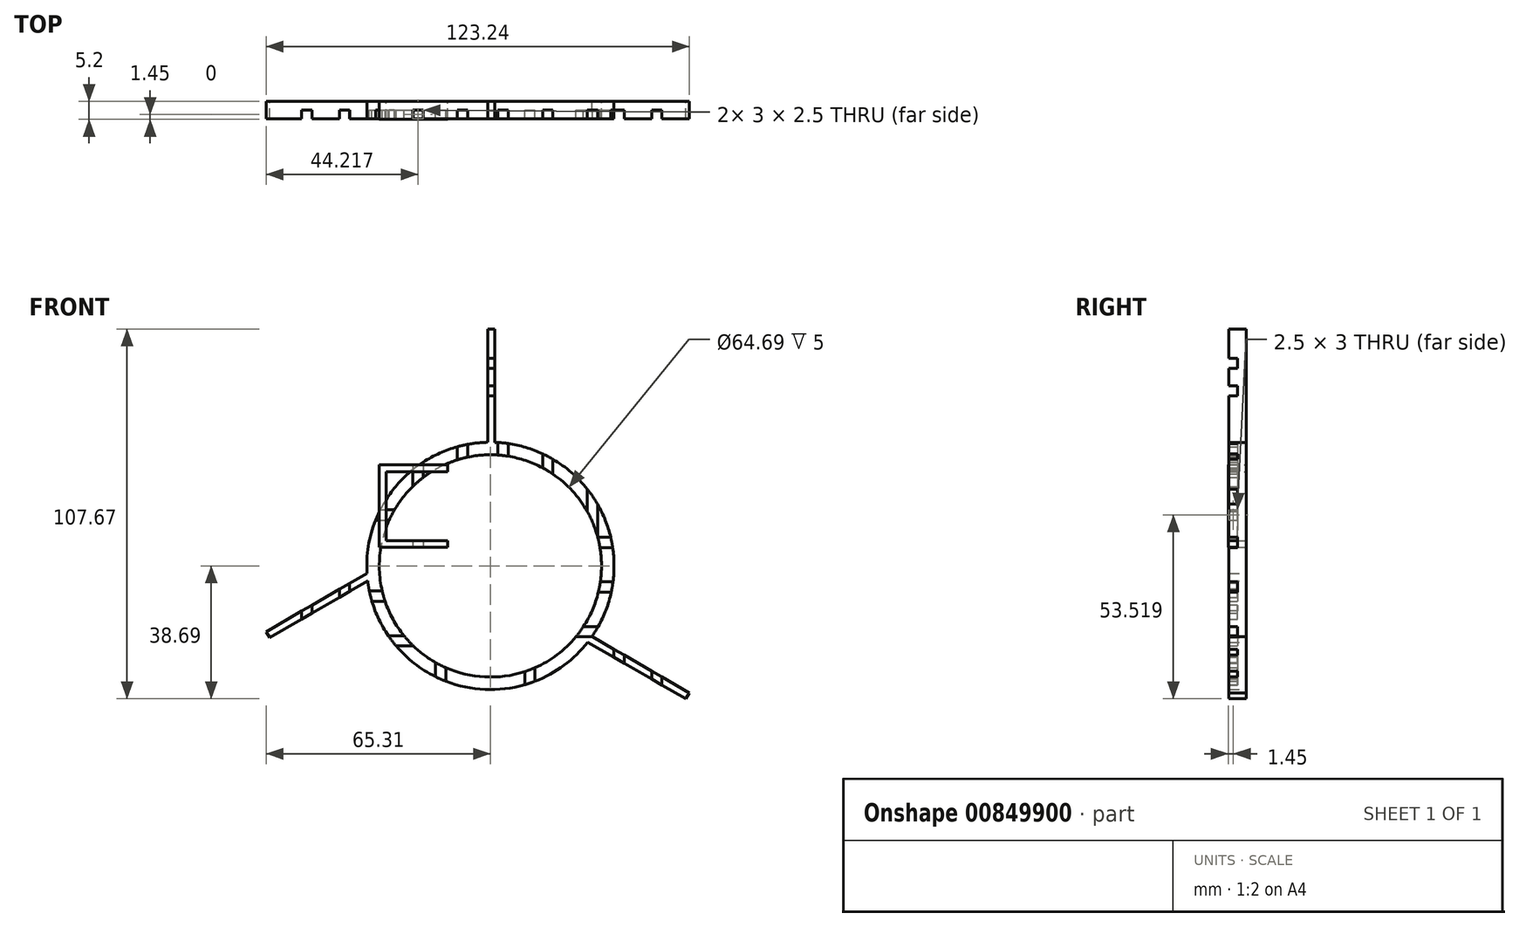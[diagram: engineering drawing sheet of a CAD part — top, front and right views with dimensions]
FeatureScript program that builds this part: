
annotation { "Feature Type Name" : "Feature", "Feature Type Description" : "" }
export const myFeature = defineFeature(function(context is Context, id is Id, definition is map)
    precondition{}
    {
        {
            var Q0;
            Q0=qCreatedBy(makeId("Front.planeOp"),FACE);
            var sketch = newSketch(context, id + "F0", { "sketchPlane" : qUnion([Q0])});
            skLineSegment(sketch, "E0.bottom", {"start": v(-32.4, 27.38) * mm, "end": v(-30.4, 27.38) * mm});
            skLineSegment(sketch, "E0.top", {"start": v(-32.4, 7.38) * mm, "end": v(-30.4, 7.38) * mm});
            skLineSegment(sketch, "E0.left", {"start": v(-32.4, 27.38) * mm, "end": v(-32.4, 7.38) * mm});
            skLineSegment(sketch, "E0.right", {"start": v(-30.4, 27.38) * mm, "end": v(-30.4, 7.38) * mm});
            skLineSegment(sketch, "E1.bottom", {"start": v(-32.4, 27.38) * mm, "end": v(-12.4, 27.38) * mm});
            skLineSegment(sketch, "E1.top", {"start": v(-32.4, 29.38) * mm, "end": v(-12.4, 29.38) * mm});
            skLineSegment(sketch, "E1.left", {"start": v(-32.4, 27.38) * mm, "end": v(-32.4, 29.38) * mm});
            skLineSegment(sketch, "E1.right", {"start": v(-12.4, 27.38) * mm, "end": v(-12.4, 29.38) * mm});
            skLineSegment(sketch, "E2.bottom", {"start": v(-32.4, 7.38) * mm, "end": v(-12.4, 7.38) * mm});
            skLineSegment(sketch, "E2.top", {"start": v(-32.4, 5.38) * mm, "end": v(-12.4, 5.38) * mm});
            skLineSegment(sketch, "E2.left", {"start": v(-32.4, 7.38) * mm, "end": v(-32.4, 5.38) * mm});
            skLineSegment(sketch, "E2.right", {"start": v(-12.4, 7.38) * mm, "end": v(-12.4, 5.38) * mm});
            skSolve(sketch);
        }
        {
            var Q0;
            Q0=makeQuery(id+"F0.imprint","IMPRINT",FACE,{"disambiguationData":[TD([[makeQuery(id+"F0.imprint","IMPRINT",EDGE,{"derivedFrom":sQuery(id+"F0.wireOp",EDGE,"E1.top")}),-1.0]])]});
            var Q1;
            {var subQ0=sQuery(id+"F0.wireOp",EDGE,"E0.left");Q1=makeQuery(id+"F0.imprint","IMPRINT",FACE,{"disambiguationData":[TD([[makeQuery(id+"F0.imprint","IMPRINT",EDGE,{"derivedFrom":subQ0}),1.0]])]});}
            var Q2;
            Q2=makeQuery(id+"F0.imprint","IMPRINT",FACE,{"disambiguationData":[TD([[makeQuery(id+"F0.imprint","IMPRINT",EDGE,{"derivedFrom":sQuery(id+"F0.wireOp",EDGE,"E2.top")}),1.0]])]});
            extrude(context, id + "F1", {"entities" : qUnion([Q0, Q1, Q2]), "depth" : 5.2 * mm, "offsetDistance" : 25 * mm});
        }
        {
            var Q0;
            Q0=qCreatedBy(makeId("Front.planeOp"),FACE);
            var sketch = newSketch(context, id + "F2", { "sketchPlane" : qUnion([Q0])});
            skCircle(sketch, "E3", {"center": v(0, 0) * mm, "radius": 36 * mm});
            skSolve(sketch);
        }
        {
            var Q0;
            Q0=makeQuery(id+"F2.imprint","IMPRINT",FACE,{"disambiguationData":[TD([[makeQuery(id+"F2.imprint","IMPRINT",EDGE,{"derivedFrom":sQuery(id+"F2.wireOp",EDGE,"E3")}),1.0]])]});
            var sketch = newSketch(context, id + "F3", { "sketchPlane" : qUnion([Q0])});
            skLineSegment(sketch, "E4", {"start": v(-0.72, 36) * mm, "end": v(-0.72, 68.98) * mm});
            skLineSegment(sketch, "E5", {"start": v(-0.72, 68.98) * mm, "end": v(1.28, 68.98) * mm});
            skLineSegment(sketch, "E6", {"start": v(1.28, 68.98) * mm, "end": v(1.28, 35.98) * mm});
            skLineSegment(sketch, "E7", {"start": v(29.55, -20.57) * mm, "end": v(57.93, -36.95) * mm});
            skLineSegment(sketch, "E8", {"start": v(57.93, -36.95) * mm, "end": v(56.93, -38.69) * mm});
            skLineSegment(sketch, "E9", {"start": v(56.93, -38.69) * mm, "end": v(28.35, -22.19) * mm});
            skLineSegment(sketch, "E10", {"start": v(-35.93, -2.18) * mm, "end": v(-65.31, -19.14) * mm});
            skLineSegment(sketch, "E11", {"start": v(-65.31, -19.14) * mm, "end": v(-64.31, -20.87) * mm});
            skLineSegment(sketch, "E12", {"start": v(-64.31, -20.87) * mm, "end": v(-35.73, -4.37) * mm});
            skCircle(sketch, "E13", {"center": v(0, 0) * mm, "radius": 36 * mm});
            skCircle(sketch, "E14", {"center": v(0, 0) * mm, "radius": 32.34 * mm});
            skSolve(sketch);
        }
        {
            var Q0;
            Q0 = qSketchRegion(id + "F3", true);
            extrude(context, id + "F4", {"entities" : qUnion([Q0]), "depth" : 5 * mm, "offsetDistance" : 25 * mm});
        }
        {
            var Q0;
            Q0=makeQuery(id+"F4.opExtrude","CAP_FACE",FACE,{"disambiguationData":[OSD([sQuery(id+"F3.wireOp",EDGE,"8RwgRzXE-qvGt-B0H7-k4Kr-Gc3pqWYvk5VT"),sQuery(id+"F3.wireOp",EDGE,"Olt6Pb1U-Hxbb-Uh9u-Cub1-vmPtMGZJXEY1"),sQuery(id+"F3.wireOp",EDGE,"KnLR224x-qTIH-nDkI-imnO-9sQnCgnEaWRT"),sQuery(id+"F3.wireOp",EDGE,"E4"),sQuery(id+"F3.wireOp",EDGE,"E5"),sQuery(id+"F3.wireOp",EDGE,"E6"),sQuery(id+"F3.wireOp",EDGE,"E7"),sQuery(id+"F3.wireOp",EDGE,"E8"),sQuery(id+"F3.wireOp",EDGE,"E9"),sQuery(id+"F3.wireOp",EDGE,"E10"),sQuery(id+"F3.wireOp",EDGE,"E11"),sQuery(id+"F3.wireOp",EDGE,"E12"),sQuery(id+"F3.wireOp",EDGE,"iQAOSqN7-Tp2O-yPxj-4RkK-xED2nn9WDPSp"),sQuery(id+"F3.wireOp",EDGE,"gfdliZdd-5jy7-NY0W-ydEy-xdDTyF2nKvZU"),sQuery(id+"F3.wireOp",EDGE,"5IQDnoGr-gjbj-nZzz-E8YA-bT8lYT3dTV5w"),sQuery(id+"F3.wireOp",EDGE,"E13"),sQuery(id+"F3.wireOp",EDGE,"E14")])],"isStart":false});
            var sketch = newSketch(context, id + "F5", { "sketchPlane" : qUnion([Q0])});
            skLineSegment(sketch, "E15.bottom", {"start": v(-57.54, 5.7) * mm, "end": v(-38.83, 5.7) * mm});
            skLineSegment(sketch, "E15.top", {"start": v(-57.54, 2.7) * mm, "end": v(-38.83, 2.7) * mm});
            skLineSegment(sketch, "E15.left", {"start": v(-57.54, 5.7) * mm, "end": v(-57.54, 2.7) * mm});
            skLineSegment(sketch, "E15.right", {"start": v(-38.83, 5.7) * mm, "end": v(-38.83, 2.7) * mm});
            skLineSegment(sketch, "E16.bottom", {"start": v(-41.23, -7.3) * mm, "end": v(-27.17, -7.3) * mm});
            skLineSegment(sketch, "E16.top", {"start": v(-41.23, -10.3) * mm, "end": v(-27.17, -10.3) * mm});
            skLineSegment(sketch, "E16.left", {"start": v(-41.23, -7.3) * mm, "end": v(-41.23, -10.3) * mm});
            skLineSegment(sketch, "E16.right", {"start": v(-27.17, -7.3) * mm, "end": v(-27.17, -10.3) * mm});
            skLineSegment(sketch, "E17.bottom", {"start": v(-36.77, -23.3) * mm, "end": v(-6.77, -23.3) * mm});
            skLineSegment(sketch, "E17.top", {"start": v(-36.77, -20.3) * mm, "end": v(-6.77, -20.3) * mm});
            skLineSegment(sketch, "E17.left", {"start": v(-36.77, -23.3) * mm, "end": v(-36.77, -20.3) * mm});
            skLineSegment(sketch, "E17.right", {"start": v(-6.77, -23.3) * mm, "end": v(-6.77, -20.3) * mm});
            skLineSegment(sketch, "E18.bottom", {"start": v(-16, -27.77) * mm, "end": v(-13, -27.77) * mm});
            skLineSegment(sketch, "E18.top", {"start": v(-16, -40.77) * mm, "end": v(-13, -40.77) * mm});
            skLineSegment(sketch, "E18.left", {"start": v(-16, -27.77) * mm, "end": v(-16, -40.77) * mm});
            skLineSegment(sketch, "E18.right", {"start": v(-13, -27.77) * mm, "end": v(-13, -40.77) * mm});
            skLineSegment(sketch, "E19.bottom", {"start": v(-3, -28.38) * mm, "end": v(0, -28.38) * mm});
            skLineSegment(sketch, "E19.top", {"start": v(-3, -43) * mm, "end": v(0, -43) * mm});
            skLineSegment(sketch, "E19.right", {"start": v(0, -28.38) * mm, "end": v(0, -43) * mm});
            skLineSegment(sketch, "E20.bottom", {"start": v(10, -10.58) * mm, "end": v(13, -10.58) * mm});
            skLineSegment(sketch, "E20.top", {"start": v(10, -40.58) * mm, "end": v(13, -40.58) * mm});
            skLineSegment(sketch, "E20.left", {"start": v(10, -10.58) * mm, "end": v(10, -40.58) * mm});
            skLineSegment(sketch, "E20.right", {"start": v(13, -10.58) * mm, "end": v(13, -40.58) * mm});
            skLineSegment(sketch, "E21.bottom", {"start": v(17.04, -17.66) * mm, "end": v(47.04, -17.66) * mm});
            skLineSegment(sketch, "E21.top", {"start": v(17.04, -20.66) * mm, "end": v(47.04, -20.66) * mm});
            skLineSegment(sketch, "E21.left", {"start": v(17.04, -17.66) * mm, "end": v(17.04, -20.66) * mm});
            skLineSegment(sketch, "E21.right", {"start": v(47.04, -17.66) * mm, "end": v(47.04, -20.66) * mm});
            skLineSegment(sketch, "E22.bottom", {"start": v(21.34, -4.66) * mm, "end": v(56.93, -4.66) * mm});
            skLineSegment(sketch, "E22.top", {"start": v(21.34, -7.66) * mm, "end": v(56.93, -7.66) * mm});
            skLineSegment(sketch, "E22.left", {"start": v(21.34, -4.66) * mm, "end": v(21.34, -7.66) * mm});
            skLineSegment(sketch, "E22.right", {"start": v(56.93, -4.66) * mm, "end": v(56.93, -7.66) * mm});
            skLineSegment(sketch, "E23.bottom", {"start": v(24.53, 8.34) * mm, "end": v(54.98, 8.34) * mm});
            skLineSegment(sketch, "E23.top", {"start": v(24.53, 5.34) * mm, "end": v(54.98, 5.34) * mm});
            skLineSegment(sketch, "E23.left", {"start": v(24.53, 8.34) * mm, "end": v(24.53, 5.34) * mm});
            skLineSegment(sketch, "E23.right", {"start": v(54.98, 8.34) * mm, "end": v(54.98, 5.34) * mm});
            skLineSegment(sketch, "E24.bottom", {"start": v(-34.5, -21) * mm, "end": v(-31.5, -21) * mm});
            skLineSegment(sketch, "E24.top", {"start": v(-41.07, -38.69) * mm, "end": v(-38.83, -38.69) * mm});
            skLineSegment(sketch, "E25.bottom", {"start": v(-9.6, 47.5) * mm, "end": v(-6.6, 47.5) * mm});
            skLineSegment(sketch, "E25.top", {"start": v(-9.6, 24.24) * mm, "end": v(-6.6, 24.24) * mm});
            skLineSegment(sketch, "E25.left", {"start": v(-9.6, 47.5) * mm, "end": v(-9.6, 24.24) * mm});
            skLineSegment(sketch, "E25.right", {"start": v(-6.6, 47.5) * mm, "end": v(-6.6, 24.24) * mm});
            skLineSegment(sketch, "E26.bottom", {"start": v(5.2, 49.48) * mm, "end": v(2.2, 49.48) * mm});
            skLineSegment(sketch, "E26.top", {"start": v(5.2, 26.4) * mm, "end": v(2.2, 26.4) * mm});
            skLineSegment(sketch, "E26.left", {"start": v(5.2, 49.48) * mm, "end": v(5.2, 26.4) * mm});
            skLineSegment(sketch, "E26.right", {"start": v(2.2, 49.48) * mm, "end": v(2.2, 26.4) * mm});
            skPoint(sketch, "E27.oppositeSnap0", {"position": v(-51.97, 22.21) * mm});
            skLineSegment(sketch, "E27.bottom", {"start": v(-54.97, -1.07) * mm, "end": v(-51.97, -1.07) * mm});
            skLineSegment(sketch, "E27.top", {"start": v(-54.97, -17.96) * mm, "end": v(-51.97, -17.96) * mm});
            skLineSegment(sketch, "E27.left", {"start": v(-54.97, -17.96) * mm, "end": v(-54.97, -1.07) * mm});
            skLineSegment(sketch, "E27.right", {"start": v(-51.97, -17.96) * mm, "end": v(-51.97, -1.07) * mm});
            skLineSegment(sketch, "E28.left", {"start": v(-23.96, 0.93) * mm, "end": v(-21.37, -0.58) * mm});
            skLineSegment(sketch, "E28.right", {"start": v(-3.3, -0.56) * mm, "end": v(-0.72, -2.07) * mm});
            skLineSegment(sketch, "E29.bottom", {"start": v(-35.93, -70.21) * mm, "end": v(-18.22, -70.21) * mm});
            skLineSegment(sketch, "E29.top", {"start": v(-35.93, -67.21) * mm, "end": v(-18.22, -67.21) * mm});
            skLineSegment(sketch, "E29.left", {"start": v(-35.93, -70.21) * mm, "end": v(-35.93, -67.21) * mm});
            skLineSegment(sketch, "E29.right", {"start": v(-18.22, -70.21) * mm, "end": v(-18.22, -67.21) * mm});
            skLineSegment(sketch, "E30.bottom", {"start": v(49.95, -4.66) * mm, "end": v(46.95, -4.66) * mm});
            skLineSegment(sketch, "E30.top", {"start": v(49.95, -41.15) * mm, "end": v(46.95, -41.15) * mm});
            skLineSegment(sketch, "E30.left", {"start": v(49.95, -4.66) * mm, "end": v(49.95, -41.15) * mm});
            skLineSegment(sketch, "E30.right", {"start": v(46.95, -4.66) * mm, "end": v(46.95, -41.15) * mm});
            skLineSegment(sketch, "E31.bottom", {"start": v(-13.56, 60.48) * mm, "end": v(8.73, 60.48) * mm});
            skLineSegment(sketch, "E31.top", {"start": v(-13.56, 57.48) * mm, "end": v(8.73, 57.48) * mm});
            skLineSegment(sketch, "E31.left", {"start": v(-13.56, 60.48) * mm, "end": v(-13.56, 57.48) * mm});
            skLineSegment(sketch, "E31.right", {"start": v(8.73, 60.48) * mm, "end": v(8.73, 57.48) * mm});
            skLineSegment(sketch, "E32.bottom", {"start": v(-22.6, 38.2) * mm, "end": v(-19.6, 38.2) * mm});
            skLineSegment(sketch, "E32.top", {"start": v(-22.6, -8.6) * mm, "end": v(-19.6, -8.6) * mm});
            skLineSegment(sketch, "E32.left", {"start": v(-22.6, 38.2) * mm, "end": v(-22.6, -8.6) * mm});
            skLineSegment(sketch, "E32.right", {"start": v(-19.6, 38.2) * mm, "end": v(-19.6, -8.6) * mm});
            skPoint(sketch, "E33", {"position": v(29.56, -67.21) * mm});
            skPoint(sketch, "E34", {"position": v(-32.98, 0.93) * mm});
            skLineSegment(sketch, "E35.bottom", {"start": v(15.2, 41.57) * mm, "end": v(18.2, 41.57) * mm});
            skLineSegment(sketch, "E35.top", {"start": v(15.2, 18.12) * mm, "end": v(18.2, 18.12) * mm});
            skLineSegment(sketch, "E35.left", {"start": v(15.2, 41.57) * mm, "end": v(15.2, 18.12) * mm});
            skLineSegment(sketch, "E35.right", {"start": v(18.2, 41.57) * mm, "end": v(18.2, 18.12) * mm});
            skLineSegment(sketch, "E36.bottom", {"start": v(28.2, 35.98) * mm, "end": v(31.2, 35.98) * mm});
            skLineSegment(sketch, "E36.top", {"start": v(28.2, 8.52) * mm, "end": v(31.2, 8.52) * mm});
            skLineSegment(sketch, "E36.left", {"start": v(28.2, 35.98) * mm, "end": v(28.2, 8.52) * mm});
            skLineSegment(sketch, "E36.right", {"start": v(31.2, 35.98) * mm, "end": v(31.2, 8.52) * mm});
            skPoint(sketch, "E37.firstSnap0", {"position": v(-0.72, 52.49) * mm});
            skLineSegment(sketch, "E37.bottom", {"start": v(-7.81, 52.49) * mm, "end": v(12, 52.49) * mm});
            skLineSegment(sketch, "E37.top", {"start": v(-7.81, 49.49) * mm, "end": v(12, 49.49) * mm});
            skLineSegment(sketch, "E37.left", {"start": v(-7.81, 52.49) * mm, "end": v(-7.81, 49.49) * mm});
            skLineSegment(sketch, "E37.right", {"start": v(12, 52.49) * mm, "end": v(12, 49.49) * mm});
            skLineSegment(sketch, "E38.bottom", {"start": v(-40.97, 12.8) * mm, "end": v(-43.97, 12.8) * mm});
            skLineSegment(sketch, "E38.top", {"start": v(-40.97, -10.98) * mm, "end": v(-43.97, -10.98) * mm});
            skLineSegment(sketch, "E38.left", {"start": v(-40.97, -10.98) * mm, "end": v(-40.97, 12.8) * mm});
            skLineSegment(sketch, "E38.right", {"start": v(-43.97, -10.98) * mm, "end": v(-43.97, 12.8) * mm});
            skLineSegment(sketch, "E39.bottom", {"start": v(35.95, -5.53) * mm, "end": v(38.95, -5.53) * mm});
            skLineSegment(sketch, "E39.top", {"start": v(35.95, -38.4) * mm, "end": v(38.95, -38.4) * mm});
            skLineSegment(sketch, "E39.left", {"start": v(35.95, -5.53) * mm, "end": v(35.95, -38.4) * mm});
            skLineSegment(sketch, "E39.right", {"start": v(38.95, -5.53) * mm, "end": v(38.95, -38.4) * mm});
            skLineSegment(sketch, "E40.bottom", {"start": v(-36.76, 16.33) * mm, "end": v(-27.3, 16.33) * mm});
            skLineSegment(sketch, "E40.top", {"start": v(-36.76, 13.33) * mm, "end": v(-27.3, 13.33) * mm});
            skLineSegment(sketch, "E40.left", {"start": v(-27.3, 16.33) * mm, "end": v(-27.3, 13.33) * mm});
            skLineSegment(sketch, "E40.right", {"start": v(-36.76, 16.33) * mm, "end": v(-36.76, 13.33) * mm});
            skLineSegment(sketch, "E41.bottom", {"start": v(-5.35, -56.21) * mm, "end": v(41.81, -56.21) * mm});
            skLineSegment(sketch, "E41.top", {"start": v(-5.35, -59.21) * mm, "end": v(41.81, -59.21) * mm});
            skLineSegment(sketch, "E41.left", {"start": v(-5.35, -56.21) * mm, "end": v(-5.35, -59.21) * mm});
            skLineSegment(sketch, "E41.right", {"start": v(41.81, -56.21) * mm, "end": v(41.81, -59.21) * mm});
            skSolve(sketch);
        }
        {
            var Q0;
            Q0 = qSketchRegion(id + "F5", true);
            extrude(context, id + "F6", {"entities" : qUnion([Q0]), "operationType" : NewBodyOperationType.REMOVE, "oppositeDirection" : true, "depth" : 2.5 * mm, "offsetDistance" : 25 * mm});
        }
    });
